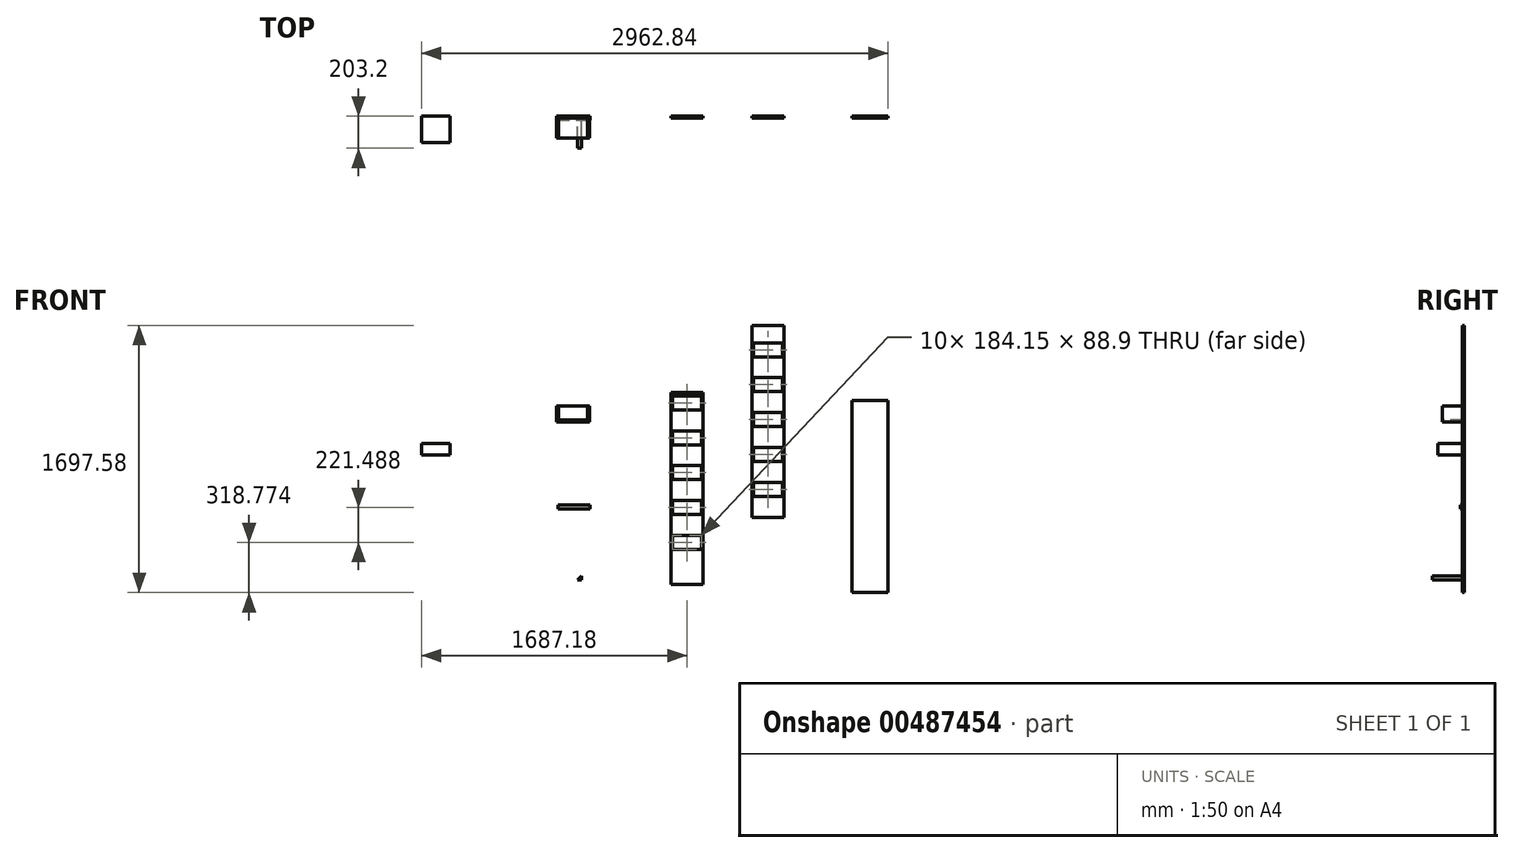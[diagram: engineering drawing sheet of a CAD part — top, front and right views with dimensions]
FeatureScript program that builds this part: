
annotation { "Feature Type Name" : "Feature", "Feature Type Description" : "" }
export const myFeature = defineFeature(function(context is Context, id is Id, definition is map)
    precondition{}
    {
        {
            var Q0;
            Q0=qCreatedBy(makeId("Front.planeOp"),FACE);
            var sketch = newSketch(context, id + "F0", { "sketchPlane" : qUnion([Q0])});
            skLineSegment(sketch, "E0.bottom", {"start": v(0, 0) * mm, "end": v(-203.2, 0) * mm});
            skLineSegment(sketch, "E0.top", {"start": v(0, 1219.2) * mm, "end": v(-203.2, 1219.2) * mm});
            skLineSegment(sketch, "E0.left", {"start": v(0, 0) * mm, "end": v(0, 1219.2) * mm});
            skLineSegment(sketch, "E0.right", {"start": v(-203.2, 0) * mm, "end": v(-203.2, 1219.2) * mm});
            skLineSegment(sketch, "E1.bottom", {"start": v(-193.68, 1197.36) * mm, "end": v(-9.53, 1197.36) * mm});
            skLineSegment(sketch, "E1.top", {"start": v(-193.68, 1108.46) * mm, "end": v(-9.53, 1108.46) * mm});
            skLineSegment(sketch, "E1.left", {"start": v(-193.68, 1197.36) * mm, "end": v(-193.68, 1108.46) * mm});
            skLineSegment(sketch, "E1.right", {"start": v(-9.53, 1197.36) * mm, "end": v(-9.53, 1108.46) * mm});
            skLineSegment(sketch, "E2.bottom", {"start": v(-193.68, 975.87) * mm, "end": v(-9.53, 975.87) * mm});
            skLineSegment(sketch, "E2.top", {"start": v(-193.68, 886.97) * mm, "end": v(-9.53, 886.97) * mm});
            skLineSegment(sketch, "E2.left", {"start": v(-193.68, 975.87) * mm, "end": v(-193.68, 886.97) * mm});
            skLineSegment(sketch, "E2.right", {"start": v(-9.53, 975.87) * mm, "end": v(-9.53, 886.97) * mm});
            skLineSegment(sketch, "E3.bottom", {"start": v(-193.67, 754.38) * mm, "end": v(-9.53, 754.38) * mm});
            skLineSegment(sketch, "E3.top", {"start": v(-193.67, 665.48) * mm, "end": v(-9.52, 665.48) * mm});
            skLineSegment(sketch, "E3.left", {"start": v(-193.67, 754.38) * mm, "end": v(-193.67, 665.48) * mm});
            skLineSegment(sketch, "E3.right", {"start": v(-9.53, 754.38) * mm, "end": v(-9.53, 665.48) * mm});
            skLineSegment(sketch, "E4.bottom", {"start": v(-193.68, 532.9) * mm, "end": v(-9.52, 532.9) * mm});
            skLineSegment(sketch, "E4.top", {"start": v(-193.68, 444) * mm, "end": v(-9.52, 444) * mm});
            skLineSegment(sketch, "E4.left", {"start": v(-193.68, 532.9) * mm, "end": v(-193.68, 444) * mm});
            skLineSegment(sketch, "E4.right", {"start": v(-9.52, 532.9) * mm, "end": v(-9.52, 444) * mm});
            skLineSegment(sketch, "E5.bottom", {"start": v(-193.67, 311.4) * mm, "end": v(-9.52, 311.4) * mm});
            skLineSegment(sketch, "E5.top", {"start": v(-193.67, 222.5) * mm, "end": v(-9.52, 222.5) * mm});
            skLineSegment(sketch, "E5.left", {"start": v(-193.67, 311.4) * mm, "end": v(-193.67, 222.5) * mm});
            skLineSegment(sketch, "E5.right", {"start": v(-9.52, 311.4) * mm, "end": v(-9.52, 222.5) * mm});
            skSolve(sketch);
        }
        {
            var Q0;
            Q0=makeQuery(id+"F0.imprint","IMPRINT",FACE,{"disambiguationData":[TD([[makeQuery(id+"F0.imprint","IMPRINT",EDGE,{"derivedFrom":sQuery(id+"F0.wireOp",EDGE,"E0.bottom")}),-1.0]])]});
            extrude(context, id + "F1", {"entities" : qUnion([Q0]), "depth" : 12.7 * mm});
        }
        {
            var Q0;
            Q0=qCreatedBy(makeId("Front.planeOp"),FACE);
            var sketch = newSketch(context, id + "F2", { "sketchPlane" : qUnion([Q0])});
            skLineSegment(sketch, "E6.bottom", {"start": v(310.08, 1645.76) * mm, "end": v(513.28, 1645.76) * mm});
            skLineSegment(sketch, "E6.top", {"start": v(310.08, 426.56) * mm, "end": v(513.28, 426.56) * mm});
            skLineSegment(sketch, "E6.left", {"start": v(310.08, 1645.76) * mm, "end": v(310.08, 426.56) * mm});
            skLineSegment(sketch, "E6.right", {"start": v(513.28, 1645.76) * mm, "end": v(513.28, 426.56) * mm});
            skLineSegment(sketch, "E7.bottom", {"start": v(319.6, 1535.02) * mm, "end": v(503.76, 1535.02) * mm});
            skLineSegment(sketch, "E7.top", {"start": v(319.6, 1446.12) * mm, "end": v(503.76, 1446.12) * mm});
            skLineSegment(sketch, "E7.left", {"start": v(319.6, 1535.02) * mm, "end": v(319.6, 1446.12) * mm});
            skLineSegment(sketch, "E7.right", {"start": v(503.76, 1535.02) * mm, "end": v(503.76, 1446.12) * mm});
            skLineSegment(sketch, "E8.bottom", {"start": v(319.6, 1313.53) * mm, "end": v(503.76, 1313.53) * mm});
            skLineSegment(sketch, "E8.top", {"start": v(319.6, 1224.63) * mm, "end": v(503.76, 1224.63) * mm});
            skLineSegment(sketch, "E8.left", {"start": v(319.6, 1313.53) * mm, "end": v(319.6, 1224.63) * mm});
            skLineSegment(sketch, "E8.right", {"start": v(503.76, 1313.53) * mm, "end": v(503.76, 1224.63) * mm});
            skLineSegment(sketch, "E9.top", {"start": v(319.6, 1003.14) * mm, "end": v(503.76, 1003.14) * mm});
            skLineSegment(sketch, "E9.left", {"start": v(319.6, 1092.04) * mm, "end": v(319.6, 1003.14) * mm});
            skLineSegment(sketch, "E9.right", {"start": v(503.76, 1092.04) * mm, "end": v(503.76, 1003.14) * mm});
            skLineSegment(sketch, "E10.bottom", {"start": v(319.6, 870.56) * mm, "end": v(503.76, 870.56) * mm});
            skLineSegment(sketch, "E10.top", {"start": v(319.6, 781.66) * mm, "end": v(503.76, 781.66) * mm});
            skLineSegment(sketch, "E10.left", {"start": v(319.6, 870.56) * mm, "end": v(319.6, 781.66) * mm});
            skLineSegment(sketch, "E10.right", {"start": v(503.76, 870.56) * mm, "end": v(503.76, 781.66) * mm});
            skLineSegment(sketch, "E11", {"start": v(319.6, 1092.04) * mm, "end": v(503.76, 1092.04) * mm});
            skLineSegment(sketch, "E12.bottom", {"start": v(319.6, 649.07) * mm, "end": v(503.76, 649.07) * mm});
            skLineSegment(sketch, "E12.top", {"start": v(319.6, 560.17) * mm, "end": v(503.76, 560.17) * mm});
            skLineSegment(sketch, "E12.left", {"start": v(319.6, 649.07) * mm, "end": v(319.6, 560.17) * mm});
            skLineSegment(sketch, "E12.right", {"start": v(503.76, 649.07) * mm, "end": v(503.76, 560.17) * mm});
            skSolve(sketch);
        }
        {
            var Q0;
            Q0=makeQuery(id+"F2.imprint","IMPRINT",FACE,{"disambiguationData":[TD([[makeQuery(id+"F2.imprint","IMPRINT",EDGE,{"derivedFrom":sQuery(id+"F2.wireOp",EDGE,"E6.bottom")}),-1.0]])]});
            extrude(context, id + "F3", {"entities" : qUnion([Q0]), "depth" : 12.7 * mm});
        }
        {
            var Q0;
            Q0=qCreatedBy(makeId("Front.planeOp"),FACE);
            var sketch = newSketch(context, id + "F4", { "sketchPlane" : qUnion([Q0])});
            skLineSegment(sketch, "E13.bottom", {"start": v(-930.56, 1132.5) * mm, "end": v(-721.01, 1132.5) * mm});
            skLineSegment(sketch, "E13.top", {"start": v(-930.56, 1030.9) * mm, "end": v(-721.01, 1030.9) * mm});
            skLineSegment(sketch, "E13.left", {"start": v(-930.56, 1132.5) * mm, "end": v(-930.56, 1030.9) * mm});
            skLineSegment(sketch, "E13.right", {"start": v(-721.01, 1132.5) * mm, "end": v(-721.01, 1030.9) * mm});
            skSolve(sketch);
        }
        {
            var Q0;
            Q0=makeQuery(id+"F4.imprint","IMPRINT",FACE,{"disambiguationData":[TD([[makeQuery(id+"F4.imprint","IMPRINT",EDGE,{"derivedFrom":sQuery(id+"F4.wireOp",EDGE,"E13.bottom")}),-1.0]])]});
            extrude(context, id + "F5", {"entities" : qUnion([Q0]), "depth" : 139.7 * mm});
        }
        {
            var Q0;
            Q0=makeQuery(id+"F5.opExtrude","SWEPT_FACE",FACE,{"disambiguationData":[OSD([sQuery(id+"F4.wireOp",EDGE,"E13.bottom")])]});
            var sketch = newSketch(context, id + "F6", { "sketchPlane" : qUnion([Q0])});
            skLineSegment(sketch, "E14.bottom", {"start": v(-917.86, -12.7) * mm, "end": v(-733.71, -12.7) * mm});
            skLineSegment(sketch, "E14.top", {"start": v(-917.86, -139.7) * mm, "end": v(-733.71, -139.7) * mm});
            skLineSegment(sketch, "E14.left", {"start": v(-917.86, -12.7) * mm, "end": v(-917.86, -139.7) * mm});
            skLineSegment(sketch, "E14.right", {"start": v(-733.71, -12.7) * mm, "end": v(-733.71, -139.7) * mm});
            skSolve(sketch);
        }
        {
            var Q0;
            Q0=makeQuery(id+"F6.imprint","IMPRINT",FACE,{"disambiguationData":[TD([[makeQuery(id+"F6.imprint","IMPRINT",EDGE,{"derivedFrom":sQuery(id+"F6.wireOp",EDGE,"E14.bottom")}),-1.0]])]});
            extrude(context, id + "F7", {"entities" : qUnion([Q0]), "operationType" : NewBodyOperationType.REMOVE, "oppositeDirection" : true, "depth" : 88.9 * mm});
        }
        {
            var Q0;
            Q0=qCreatedBy(makeId("Front.planeOp"),FACE);
            var sketch = newSketch(context, id + "F8", { "sketchPlane" : qUnion([Q0])});
            skLineSegment(sketch, "E15.bottom", {"start": v(-922.44, 506.66) * mm, "end": v(-719.24, 506.66) * mm});
            skLineSegment(sketch, "E15.top", {"start": v(-922.44, 481.26) * mm, "end": v(-719.24, 481.26) * mm});
            skLineSegment(sketch, "E15.left", {"start": v(-922.44, 506.66) * mm, "end": v(-922.44, 481.26) * mm});
            skLineSegment(sketch, "E15.right", {"start": v(-719.24, 506.66) * mm, "end": v(-719.24, 481.26) * mm});
            skSolve(sketch);
        }
        {
            var Q0;
            Q0=makeQuery(id+"F8.imprint","IMPRINT",FACE,{"disambiguationData":[TD([[makeQuery(id+"F8.imprint","IMPRINT",EDGE,{"derivedFrom":sQuery(id+"F8.wireOp",EDGE,"E15.bottom")}),-1.0]])]});
            extrude(context, id + "F9", {"entities" : qUnion([Q0]), "depth" : 25.4 * mm});
        }
        {
            var Q0;
            Q0=qCreatedBy(makeId("Front.planeOp"),FACE);
            var sketch = newSketch(context, id + "F10", { "sketchPlane" : qUnion([Q0])});
            skLineSegment(sketch, "E16.bottom", {"start": v(-1788.78, 896.63) * mm, "end": v(-1607.8, 896.63) * mm});
            skLineSegment(sketch, "E16.top", {"start": v(-1788.78, 823.6) * mm, "end": v(-1607.8, 823.6) * mm});
            skLineSegment(sketch, "E16.left", {"start": v(-1788.78, 896.63) * mm, "end": v(-1788.78, 823.6) * mm});
            skLineSegment(sketch, "E16.right", {"start": v(-1607.8, 896.63) * mm, "end": v(-1607.8, 823.6) * mm});
            skSolve(sketch);
        }
        {
            var Q0;
            Q0=makeQuery(id+"F10.imprint","IMPRINT",FACE,{"disambiguationData":[TD([[makeQuery(id+"F10.imprint","IMPRINT",EDGE,{"derivedFrom":sQuery(id+"F10.wireOp",EDGE,"E16.bottom")}),-1.0]])]});
            extrude(context, id + "F11", {"entities" : qUnion([Q0]), "depth" : 168.27 * mm});
        }
        {
            var Q0;
            Q0=qCreatedBy(makeId("Front.planeOp"),FACE);
            var sketch = newSketch(context, id + "F12", { "sketchPlane" : qUnion([Q0])});
            skLineSegment(sketch, "E17.bottom", {"start": v(945.46, 1167.38) * mm, "end": v(1174.06, 1167.38) * mm});
            skLineSegment(sketch, "E17.top", {"start": v(945.46, -51.82) * mm, "end": v(1174.06, -51.82) * mm});
            skLineSegment(sketch, "E17.left", {"start": v(945.46, 1167.38) * mm, "end": v(945.46, -51.82) * mm});
            skLineSegment(sketch, "E17.right", {"start": v(1174.06, 1167.38) * mm, "end": v(1174.06, -51.82) * mm});
            skSolve(sketch);
        }
        {
            var Q0;
            Q0=makeQuery(id+"F12.imprint","IMPRINT",FACE,{"disambiguationData":[TD([[makeQuery(id+"F12.imprint","IMPRINT",EDGE,{"derivedFrom":sQuery(id+"F12.wireOp",EDGE,"E17.bottom")}),-1.0]])]});
            extrude(context, id + "F13", {"entities" : qUnion([Q0]), "depth" : 12.7 * mm});
        }
        {
            var Q0;
            Q0=qCreatedBy(makeId("Front.planeOp"),FACE);
            var sketch = newSketch(context, id + "F14", { "sketchPlane" : qUnion([Q0])});
            skLineSegment(sketch, "E18", {"start": v(-771.36, 55.69) * mm, "end": v(-771.36, 30.29) * mm});
            skLineSegment(sketch, "E19", {"start": v(-771.36, 30.29) * mm, "end": v(-796.76, 30.29) * mm});
            skLineSegment(sketch, "E20", {"start": v(-796.76, 30.29) * mm, "end": v(-771.36, 55.69) * mm});
            skSolve(sketch);
        }
        {
            var Q0;
            Q0=makeQuery(id+"F14.imprint","IMPRINT",FACE,{"disambiguationData":[TD([[makeQuery(id+"F14.imprint","IMPRINT",EDGE,{"derivedFrom":sQuery(id+"F14.wireOp",EDGE,"E18")}),-1.0]])]});
            extrude(context, id + "F15", {"entities" : qUnion([Q0]), "depth" : 203.2 * mm});
        }
    });
